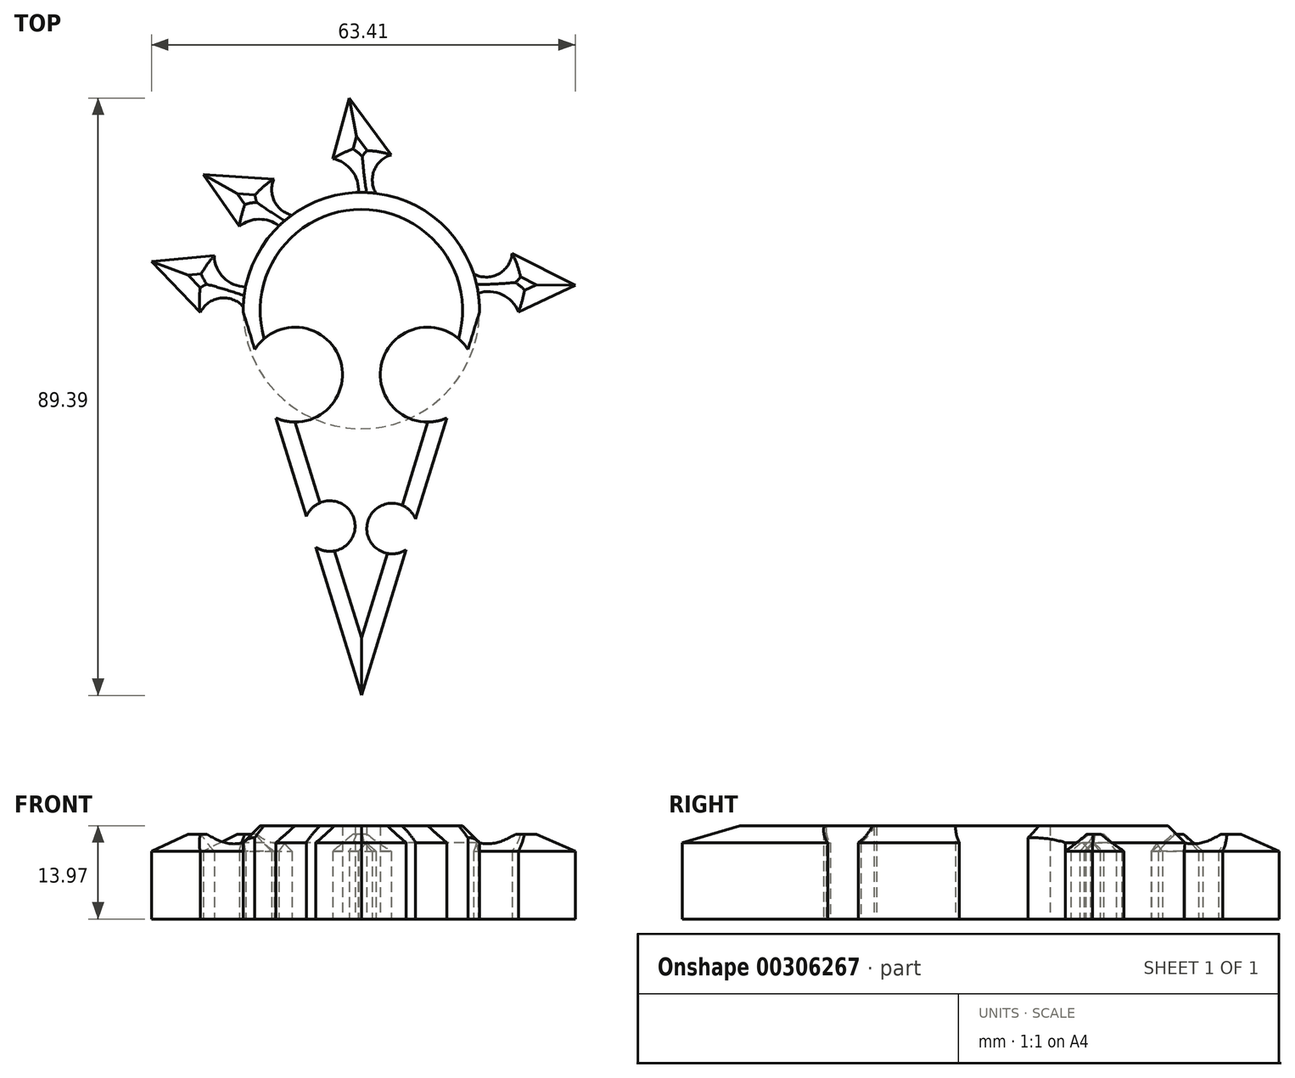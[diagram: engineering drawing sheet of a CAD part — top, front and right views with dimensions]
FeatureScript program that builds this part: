
annotation { "Feature Type Name" : "Feature", "Feature Type Description" : "" }
export const myFeature = defineFeature(function(context is Context, id is Id, definition is map)
    precondition{}
    {
        {
            var Q0;
            Q0=qCreatedBy(makeId("Top.planeOp"),FACE);
            var sketch = newSketch(context, id + "F0", { "sketchPlane" : qUnion([Q0])});
            skLineSegment(sketch, "E0", {"start": v(-44.47, -5.9) * mm, "end": v(-51.3, 16.29) * mm});
            skLineSegment(sketch, "E1", {"start": v(-26.78, 51.48) * mm, "end": v(-28.52, 45.85) * mm});
            skArc(sketch, "E2", {"start": v(-26.78, 51.48) * mm, "mid": v(-44.47, 69.36) * mm, "end": v(-62.15, 51.48) * mm});
            skArc(sketch, "E3", {"start": v(-36.34, 20.46) * mm, "mid": v(-43.47, 20.17) * mm, "end": v(-37.74, 15.92) * mm});
            skArc(sketch, "E4.MirrorCS", {"start": v(-52.7, 20.83) * mm, "mid": v(-45.57, 20.54) * mm, "end": v(-51.3, 16.29) * mm});
            skArc(sketch, "E5", {"start": v(-57.26, 35.6) * mm, "mid": v(-47.6, 44.19) * mm, "end": v(-60.42, 45.85) * mm});
            skArc(sketch, "E6.MirrorCS", {"start": v(-31.67, 35.6) * mm, "mid": v(-41.33, 44.19) * mm, "end": v(-28.52, 45.85) * mm});
            skPoint(sketch, "E7", {"position": v(-44.47, 69.36) * mm});
            skArc(sketch, "E8", {"start": v(-27.66, 57.18) * mm, "mid": v(-23.97, 57.14) * mm, "end": v(-21.9, 60.2) * mm});
            skArc(sketch, "E9", {"start": v(-20.96, 51.48) * mm, "mid": v(-23.4, 54.09) * mm, "end": v(-26.97, 54.26) * mm});
            skLineSegment(sketch, "E10", {"start": v(-21.9, 60.2) * mm, "end": v(-12.45, 55.49) * mm});
            skLineSegment(sketch, "E11", {"start": v(-12.45, 55.49) * mm, "end": v(-20.96, 51.48) * mm});
            skArc(sketch, "E12.4.0", {"start": v(-62.14, 52.25) * mm, "mid": v(-65.6, 53.55) * mm, "end": v(-68.58, 51.38) * mm});
            skLineSegment(sketch, "E12.4.1", {"start": v(-68.58, 51.38) * mm, "end": v(-75.86, 59.04) * mm});
            skLineSegment(sketch, "E12.4.2", {"start": v(-75.86, 59.04) * mm, "end": v(-66.5, 59.9) * mm});
            skArc(sketch, "E12.4.3", {"start": v(-66.5, 59.9) * mm, "mid": v(-65.09, 56.61) * mm, "end": v(-61.8, 55.23) * mm});
            skArc(sketch, "E13.MirrorCS", {"start": v(-62.73, 64.3) * mm, "mid": v(-59.3, 65.33) * mm, "end": v(-56.13, 63.69) * mm});
            skLineSegment(sketch, "E14.MirrorCS", {"start": v(-68.1, 72.02) * mm, "end": v(-62.73, 64.3) * mm});
            skLineSegment(sketch, "E15.MirrorCS", {"start": v(-57.55, 71.36) * mm, "end": v(-68.1, 72.02) * mm});
            skArc(sketch, "E16.MirrorCS", {"start": v(-54.08, 65.87) * mm, "mid": v(-57.29, 67.68) * mm, "end": v(-57.55, 71.36) * mm});
            skArc(sketch, "E17.MirrorCS", {"start": v(-48.74, 74.4) * mm, "mid": v(-45.75, 72.45) * mm, "end": v(-44.96, 68.96) * mm});
            skArc(sketch, "E18.MirrorCS", {"start": v(-41.97, 68.8) * mm, "mid": v(-42.64, 72.42) * mm, "end": v(-39.99, 74.98) * mm});
            skLineSegment(sketch, "E19.MirrorCS", {"start": v(-46.27, 83.48) * mm, "end": v(-48.74, 74.4) * mm});
            skLineSegment(sketch, "E20.MirrorCS", {"start": v(-39.99, 74.98) * mm, "end": v(-46.27, 83.48) * mm});
            skArc(sketch, "E21.MirrorCS", {"start": v(-32.28, 73.23) * mm, "mid": v(-32.16, 69.3) * mm, "end": v(-35.03, 66.63) * mm});
            skLineSegment(sketch, "E22.MirrorCS", {"start": v(-23.74, 77.17) * mm, "end": v(-32.28, 73.23) * mm});
            skLineSegment(sketch, "E23.MirrorCS", {"start": v(-26.2, 66.9) * mm, "end": v(-23.74, 77.17) * mm});
            skArc(sketch, "E24.MirrorCS", {"start": v(-32.22, 64.44) * mm, "mid": v(-29.88, 67.28) * mm, "end": v(-26.2, 66.9) * mm});
            skLineSegment(sketch, "E25.trimOffspring", {"start": v(-60.42, 45.85) * mm, "end": v(-62.15, 51.48) * mm});
            skLineSegment(sketch, "E26.trimOffspring", {"start": v(-31.67, 35.6) * mm, "end": v(-36.34, 20.46) * mm});
            skLineSegment(sketch, "E27.trimOffspring", {"start": v(-37.74, 15.92) * mm, "end": v(-44.47, -5.9) * mm});
            skLineSegment(sketch, "E28.trimOffspring", {"start": v(-52.7, 20.83) * mm, "end": v(-57.26, 35.6) * mm});
            skSolve(sketch);
        }
        {
            var Q0;
            {var subQ0=sQuery(id+"F0.wireOp",EDGE,"E12.4.0");Q0=makeQuery(id+"F0.imprint","IMPRINT",FACE,{"disambiguationData":[TD([[makeQuery(id+"F0.imprint","IMPRINT",EDGE,{"derivedFrom":subQ0}),-1.0]])]});}
            var Q1;
            {var subQ1=sQuery(id+"F0.wireOp",EDGE,"E14.MirrorCS");Q1=makeQuery(id+"F0.imprint","IMPRINT",FACE,{"disambiguationData":[TD([[makeQuery(id+"F0.imprint","IMPRINT",EDGE,{"derivedFrom":subQ1}),1.0]])]});}
            var Q2;
            {var subQ0=sQuery(id+"F0.wireOp",EDGE,"E19.MirrorCS");Q2=makeQuery(id+"F0.imprint","IMPRINT",FACE,{"disambiguationData":[TD([[makeQuery(id+"F0.imprint","IMPRINT",EDGE,{"derivedFrom":subQ0}),1.0]])]});}
            var Q3;
            {var subQ0=sQuery(id+"F0.wireOp",EDGE,"E21.MirrorCS");Q3=makeQuery(id+"F0.imprint","IMPRINT",FACE,{"disambiguationData":[TD([[makeQuery(id+"F0.imprint","IMPRINT",EDGE,{"derivedFrom":subQ0}),1.0]])]});}
            var Q4;
            {var subQ0=sQuery(id+"F0.wireOp",EDGE,"E8");Q4=makeQuery(id+"F0.imprint","IMPRINT",FACE,{"disambiguationData":[TD([[makeQuery(id+"F0.imprint","IMPRINT",EDGE,{"derivedFrom":subQ0}),-1.0]])]});}
            extrude(context, id + "F1", {"entities" : qUnion([Q0, Q1, Q2, Q3, Q4]), "depth" : 12.7 * mm});
        }
        {
            var Q0;
            Q0=makeQuery(id+"F0.imprint","IMPRINT",FACE,{"disambiguationData":[TD([[makeQuery(id+"F0.imprint","IMPRINT",EDGE,{"derivedFrom":sQuery(id+"F0.wireOp",EDGE,"E0")}),-1.0]])]});
            extrude(context, id + "F2", {"entities" : qUnion([Q0]), "depth" : 13.97 * mm});
        }
        {
            var Q0;
            Q0=makeQuery(id+"F2.opExtrude","CAP_EDGE",EDGE,{"disambiguationData":[OSD([sQuery(id+"F0.wireOp",EDGE,"E2")])],"isStart":false});
            var Q1;
            Q1=makeQuery(id+"F2.opExtrude","CAP_EDGE",EDGE,{"disambiguationData":[OSD([sQuery(id+"F0.wireOp",EDGE,"E26.trimOffspring")])],"isStart":false});
            var Q2;
            Q2=makeQuery(id+"F2.opExtrude","CAP_EDGE",EDGE,{"disambiguationData":[OSD([sQuery(id+"F0.wireOp",EDGE,"E28.trimOffspring")])],"isStart":false});
            var Q3;
            Q3=makeQuery(id+"F2.opExtrude","CAP_EDGE",EDGE,{"disambiguationData":[OSD([sQuery(id+"F0.wireOp",EDGE,"E0")])],"isStart":false});
            var Q4;
            Q4=makeQuery(id+"F2.opExtrude","CAP_EDGE",EDGE,{"disambiguationData":[OSD([sQuery(id+"F0.wireOp",EDGE,"E27.trimOffspring")])],"isStart":false});
            chamfer(context, id + "F3", {"entities" : qUnion([Q0, Q1, Q2, Q3, Q4]), "width" : 2.54 * mm, "tangentPropagation" : true});
        }
        {
            var Q0;
            Q0=makeQuery(id+"F1.opExtrude","CAP_EDGE",EDGE,{"disambiguationData":[OSD([sQuery(id+"F0.wireOp",EDGE,"E10")])],"isStart":false});
            var Q1;
            Q1=makeQuery(id+"F1.opExtrude","CAP_EDGE",EDGE,{"disambiguationData":[OSD([sQuery(id+"F0.wireOp",EDGE,"E11")])],"isStart":false});
            var Q2;
            Q2=makeQuery(id+"F1.opExtrude","CAP_EDGE",EDGE,{"disambiguationData":[OSD([sQuery(id+"F0.wireOp",EDGE,"E8")])],"isStart":false});
            var Q3;
            Q3=makeQuery(id+"F1.opExtrude","CAP_EDGE",EDGE,{"disambiguationData":[OSD([sQuery(id+"F0.wireOp",EDGE,"E9")])],"isStart":false});
            var Q4;
            Q4=makeQuery(id+"F1.opExtrude","CAP_EDGE",EDGE,{"disambiguationData":[OSD([sQuery(id+"F0.wireOp",EDGE,"E23.MirrorCS")])],"isStart":false});
            var Q5;
            Q5=makeQuery(id+"F1.opExtrude","CAP_EDGE",EDGE,{"disambiguationData":[OSD([sQuery(id+"F0.wireOp",EDGE,"E22.MirrorCS")])],"isStart":false});
            var Q6;
            Q6=makeQuery(id+"F1.opExtrude","CAP_EDGE",EDGE,{"disambiguationData":[OSD([sQuery(id+"F0.wireOp",EDGE,"E21.MirrorCS")])],"isStart":false});
            var Q7;
            Q7=makeQuery(id+"F1.opExtrude","CAP_EDGE",EDGE,{"disambiguationData":[OSD([sQuery(id+"F0.wireOp",EDGE,"E24.MirrorCS")])],"isStart":false});
            var Q8;
            Q8=makeQuery(id+"F1.opExtrude","CAP_EDGE",EDGE,{"disambiguationData":[OSD([sQuery(id+"F0.wireOp",EDGE,"E20.MirrorCS")])],"isStart":false});
            var Q9;
            Q9=makeQuery(id+"F1.opExtrude","CAP_EDGE",EDGE,{"disambiguationData":[OSD([sQuery(id+"F0.wireOp",EDGE,"E19.MirrorCS")])],"isStart":false});
            var Q10;
            Q10=makeQuery(id+"F1.opExtrude","CAP_EDGE",EDGE,{"disambiguationData":[OSD([sQuery(id+"F0.wireOp",EDGE,"E17.MirrorCS")])],"isStart":false});
            var Q11;
            Q11=makeQuery(id+"F1.opExtrude","CAP_EDGE",EDGE,{"disambiguationData":[OSD([sQuery(id+"F0.wireOp",EDGE,"E18.MirrorCS")])],"isStart":false});
            var Q12;
            Q12=makeQuery(id+"F1.opExtrude","CAP_EDGE",EDGE,{"disambiguationData":[OSD([sQuery(id+"F0.wireOp",EDGE,"E15.MirrorCS")])],"isStart":false});
            var Q13;
            Q13=makeQuery(id+"F1.opExtrude","CAP_EDGE",EDGE,{"disambiguationData":[OSD([sQuery(id+"F0.wireOp",EDGE,"E16.MirrorCS")])],"isStart":false});
            var Q14;
            Q14=makeQuery(id+"F1.opExtrude","CAP_EDGE",EDGE,{"disambiguationData":[OSD([sQuery(id+"F0.wireOp",EDGE,"E13.MirrorCS")])],"isStart":false});
            var Q15;
            Q15=makeQuery(id+"F1.opExtrude","CAP_EDGE",EDGE,{"disambiguationData":[OSD([sQuery(id+"F0.wireOp",EDGE,"E14.MirrorCS")])],"isStart":false});
            var Q16;
            Q16=makeQuery(id+"F1.opExtrude","CAP_EDGE",EDGE,{"disambiguationData":[OSD([sQuery(id+"F0.wireOp",EDGE,"E12.4.2")])],"isStart":false});
            var Q17;
            Q17=makeQuery(id+"F1.opExtrude","CAP_EDGE",EDGE,{"disambiguationData":[OSD([sQuery(id+"F0.wireOp",EDGE,"E12.4.1")])],"isStart":false});
            var Q18;
            Q18=makeQuery(id+"F1.opExtrude","CAP_EDGE",EDGE,{"disambiguationData":[OSD([sQuery(id+"F0.wireOp",EDGE,"E12.4.0")])],"isStart":false});
            var Q19;
            Q19=makeQuery(id+"F1.opExtrude","CAP_EDGE",EDGE,{"disambiguationData":[OSD([sQuery(id+"F0.wireOp",EDGE,"E12.4.3")])],"isStart":false});
            chamfer(context, id + "F4", {"entities" : qUnion([Q0, Q1, Q2, Q3, Q4, Q5, Q6, Q7, Q8, Q9, Q10, Q11, Q12, Q13, Q14, Q15, Q16, Q17, Q18, Q19]), "width" : 2.54 * mm, "tangentPropagation" : true});
        }
    });
